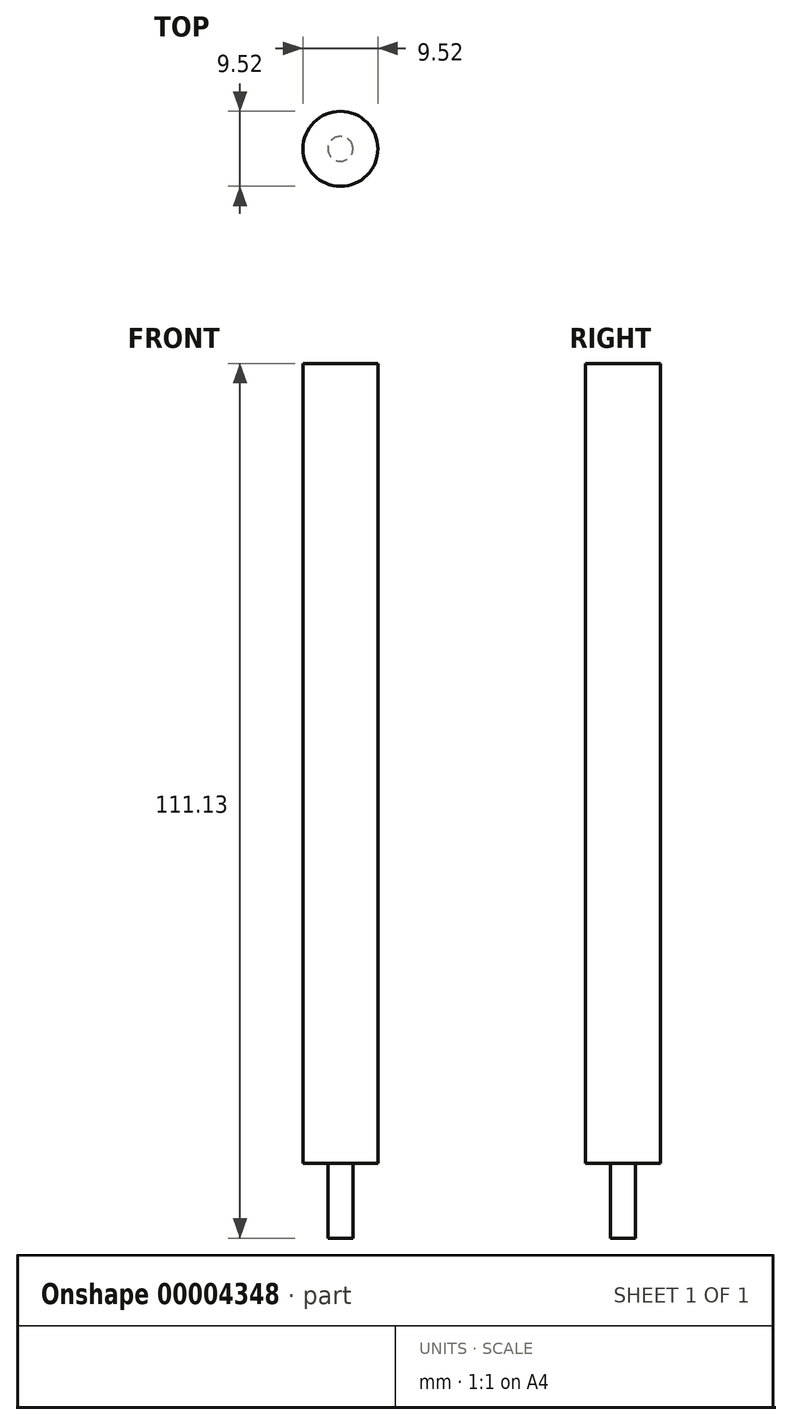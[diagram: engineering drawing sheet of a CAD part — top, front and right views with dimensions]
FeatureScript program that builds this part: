
annotation { "Feature Type Name" : "Feature", "Feature Type Description" : "" }
export const myFeature = defineFeature(function(context is Context, id is Id, definition is map)
    precondition{}
    {
        {
            var Q0;
            Q0=qCreatedBy(makeId("Top.planeOp"),FACE);
            var sketch = newSketch(context, id + "F0", { "sketchPlane" : qUnion([Q0])});
            skCircle(sketch, "E0", {"center": v(0, 0) * mm, "radius": 4.76 * mm});
            skCircle(sketch, "E1", {"center": v(0, 0) * mm, "radius": 1.59 * mm});
            skSolve(sketch);
        }
        {
            var Q0;
            Q0=makeQuery(id+"F0.imprint","IMPRINT",FACE,{"disambiguationData":[TD([[makeQuery(id+"F0.imprint","IMPRINT",EDGE,{"derivedFrom":sQuery(id+"F0.wireOp",EDGE,"E0")}),1.0]])]});
            var Q1;
            Q1=makeQuery(id+"F0.imprint","IMPRINT",FACE,{"disambiguationData":[TD([[makeQuery(id+"F0.imprint","IMPRINT",EDGE,{"derivedFrom":sQuery(id+"F0.wireOp",EDGE,"E1")}),1.0]])]});
            extrude(context, id + "F1", {"entities" : qUnion([Q0, Q1]), "depth" : 101.6 * mm});
        }
        {
            var Q0;
            Q0=makeQuery(id+"F0.imprint","IMPRINT",FACE,{"disambiguationData":[TD([[makeQuery(id+"F0.imprint","IMPRINT",EDGE,{"derivedFrom":sQuery(id+"F0.wireOp",EDGE,"E1")}),1.0]])]});
            extrude(context, id + "F2", {"entities" : qUnion([Q0]), "operationType" : NewBodyOperationType.ADD, "oppositeDirection" : true, "depth" : 9.52 * mm});
        }
    });
